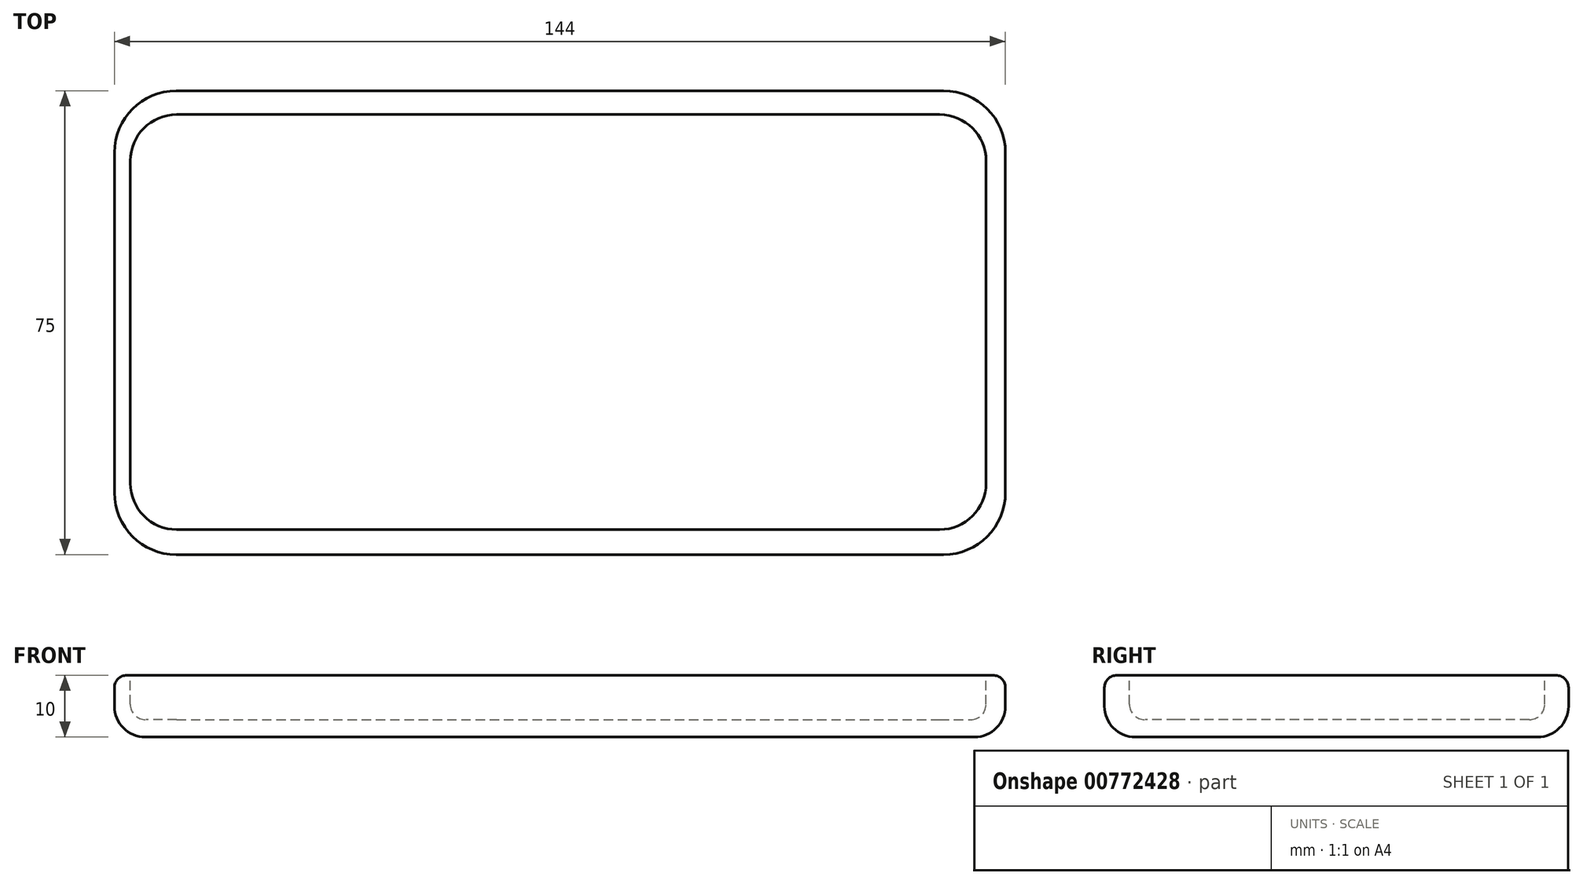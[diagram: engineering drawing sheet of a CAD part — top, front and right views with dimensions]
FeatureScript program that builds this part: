
annotation { "Feature Type Name" : "Feature", "Feature Type Description" : "" }
export const myFeature = defineFeature(function(context is Context, id is Id, definition is map)
    precondition{}
    {
        {
            var Q0;
            Q0=qCreatedBy(makeId("Top.planeOp"),FACE);
            var sketch = newSketch(context, id + "F0", { "sketchPlane" : qUnion([Q0])});
            skLineSegment(sketch, "E0.bottom", {"start": v(-137.75, 28.6) * mm, "end": v(6.25, 28.6) * mm});
            skLineSegment(sketch, "E0.top", {"start": v(-137.75, -43.4) * mm, "end": v(6.25, -43.4) * mm});
            skLineSegment(sketch, "E0.left", {"start": v(-137.75, 28.6) * mm, "end": v(-137.75, -43.4) * mm});
            skLineSegment(sketch, "E0.right", {"start": v(6.25, 28.6) * mm, "end": v(6.25, -43.4) * mm});
            skSolve(sketch);
        }
        {
            var Q0;
            Q0=makeQuery(id+"F0.imprint","IMPRINT",FACE,{"disambiguationData":[TD([[makeQuery(id+"F0.imprint","IMPRINT",EDGE,{"derivedFrom":sQuery(id+"F0.wireOp",EDGE,"E0.bottom")}),-1.0]])]});
            extrude(context, id + "F1", {"entities" : qUnion([Q0]), "depth" : 10 * mm, "offsetDistance" : 25 * mm});
        }
        {
            var Q0;
            Q0=makeQuery(id+"F1.opExtrude","CAP_FACE",FACE,{"disambiguationData":[OSD([sQuery(id+"F0.wireOp",EDGE,"E0.bottom"),sQuery(id+"F0.wireOp",EDGE,"E0.top"),sQuery(id+"F0.wireOp",EDGE,"E0.left"),sQuery(id+"F0.wireOp",EDGE,"E0.right")])],"isStart":false});
            var sketch = newSketch(context, id + "F2", { "sketchPlane" : qUnion([Q0])});
            skLineSegment(sketch, "E1.bottom", {"start": v(-135.18, 27.75) * mm, "end": v(3.12, 27.75) * mm});
            skLineSegment(sketch, "E1.top", {"start": v(-135.18, -39.35) * mm, "end": v(3.12, -39.35) * mm});
            skLineSegment(sketch, "E1.left", {"start": v(-135.18, 27.75) * mm, "end": v(-135.18, -39.35) * mm});
            skLineSegment(sketch, "E1.right", {"start": v(3.12, 27.75) * mm, "end": v(3.12, -39.35) * mm});
            skSolve(sketch);
        }
        {
            var Q0;
            Q0=makeQuery(id+"F1.opExtrude","SWEPT_FACE",FACE,{"disambiguationData":[OSD([sQuery(id+"F0.wireOp",EDGE,"E0.bottom")])]});
            extrude(context, id + "F3", {"entities" : qUnion([Q0]), "operationType" : NewBodyOperationType.ADD, "depth" : 3 * mm, "offsetDistance" : 25 * mm});
        }
        {
            var Q0;
            Q0=makeQuery(id+"F2.imprint","IMPRINT",FACE,{"disambiguationData":[TD([[makeQuery(id+"F2.imprint","IMPRINT",EDGE,{"derivedFrom":sQuery(id+"F2.wireOp",EDGE,"E1.bottom")}),-1.0]])]});
            extrude(context, id + "F4", {"entities" : qUnion([Q0]), "operationType" : NewBodyOperationType.REMOVE, "oppositeDirection" : true, "depth" : 7.2 * mm, "offsetDistance" : 25 * mm});
        }
        {
            var Q0;
            Q0=makeQuery(id+"F4.boolean.opBoolean","COPY",EDGE,{"derivedFrom":makeQuery(id+"F4.opExtrude","SWEPT_EDGE",EDGE,{"disambiguationData":[OSD([sQuery(id+"F2.wireOp",EDGE,"E1.bottom"),sQuery(id+"F2.wireOp",EDGE,"E1.left")])]})});
            var Q1;
            Q1=makeQuery(id+"F4.boolean.opBoolean","COPY",EDGE,{"derivedFrom":makeQuery(id+"F4.opExtrude","SWEPT_EDGE",EDGE,{"disambiguationData":[OSD([sQuery(id+"F2.wireOp",EDGE,"E1.top"),sQuery(id+"F2.wireOp",EDGE,"E1.left")])]})});
            var Q2;
            Q2=makeQuery(id+"F4.boolean.opBoolean","COPY",EDGE,{"derivedFrom":makeQuery(id+"F4.opExtrude","SWEPT_EDGE",EDGE,{"disambiguationData":[OSD([sQuery(id+"F2.wireOp",EDGE,"E1.top"),sQuery(id+"F2.wireOp",EDGE,"E1.right")])]})});
            var Q3;
            Q3=makeQuery(id+"F4.boolean.opBoolean","COPY",EDGE,{"derivedFrom":makeQuery(id+"F4.opExtrude","SWEPT_EDGE",EDGE,{"disambiguationData":[OSD([sQuery(id+"F2.wireOp",EDGE,"E1.bottom"),sQuery(id+"F2.wireOp",EDGE,"E1.right")])]})});
            fillet(context, id + "F5", {"entities" : qUnion([Q0, Q1, Q2, Q3]), "radius" : 7.5 * mm, "tangentPropagation" : true, "allowEdgeOverflow" : false});
        }
        {
            var Q0;
            Q0=makeQuery(id+"F4.boolean.opBoolean","COPY",EDGE,{"derivedFrom":makeQuery(id+"F4.opExtrude","CAP_EDGE",EDGE,{"disambiguationData":[OSD([sQuery(id+"F2.wireOp",EDGE,"E1.bottom")])],"isStart":false})});
            fillet(context, id + "F6", {"entities" : qUnion([Q0]), "radius" : 2.5 * mm, "tangentPropagation" : true, "allowEdgeOverflow" : false});
        }
        {
            var Q0;
            Q0=makeQuery(id+"F1.opExtrude","SWEPT_EDGE",EDGE,{"disambiguationData":[OSD([sQuery(id+"F0.wireOp",EDGE,"E0.top"),sQuery(id+"F0.wireOp",EDGE,"E0.left")])]});
            var Q1;
            Q1=makeQuery(id+"F1.opExtrude","SWEPT_EDGE",EDGE,{"disambiguationData":[OSD([sQuery(id+"F0.wireOp",EDGE,"E0.top"),sQuery(id+"F0.wireOp",EDGE,"E0.right")])]});
            var Q2;
            Q2=makeQuery(id+"F3.opExtrude","CAP_EDGE",EDGE,{"disambiguationData":[OSD([sQuery(id+"F0.wireOp",EDGE,"E0.bottom"),sQuery(id+"F0.wireOp",EDGE,"E0.right")])],"isStart":false});
            var Q3;
            Q3=makeQuery(id+"F3.opExtrude","CAP_EDGE",EDGE,{"disambiguationData":[OSD([sQuery(id+"F0.wireOp",EDGE,"E0.bottom"),sQuery(id+"F0.wireOp",EDGE,"E0.left")])],"isStart":false});
            fillet(context, id + "F7", {"entities" : qUnion([Q0, Q1, Q2, Q3]), "radius" : 10 * mm, "tangentPropagation" : true, "allowEdgeOverflow" : false});
        }
        {
            var Q0;
            Q0=makeQuery(id+"F1.opExtrude","CAP_EDGE",EDGE,{"disambiguationData":[OSD([sQuery(id+"F0.wireOp",EDGE,"E0.top")])],"isStart":false});
            var Q1;
            {var subQ0=sQuery(id+"F0.wireOp",EDGE,"E0.bottom");Q1=makeQuery(id+"F3.opExtrude","CAP_EDGE",EDGE,{"disambiguationData":[OSD([subQ0]),TDD([makeQuery(id+"F1.opExtrude","CAP_EDGE",EDGE,{"disambiguationData":[OSD([subQ0])],"isStart":false})])],"isStart":false});}
            var Q2;
            {var subQ0=sQuery(id+"F0.wireOp",EDGE,"E0.left");var subQ1=sQuery(id+"F0.wireOp",EDGE,"E0.bottom");Q2=makeQuery(id+"F3.boolean.opBoolean","MERGE",EDGE,{"derivedFrom":[makeQuery(id+"F1.opExtrude","CAP_EDGE",EDGE,{"disambiguationData":[OSD([subQ0])],"isStart":false}),makeQuery(id+"F3.opExtrude","SWEPT_EDGE",EDGE,{"disambiguationData":[OSD([subQ1,subQ0]),TDD([makeQuery(id+"F1.opExtrude","CAP_VERTEX",VERTEX,{"disambiguationData":[OSD([subQ1,subQ0])],"isStart":false})])]})]});}
            fillet(context, id + "F8", {"entities" : qUnion([Q0, Q1, Q2]), "radius" : 2 * mm, "tangentPropagation" : true, "allowEdgeOverflow" : false});
        }
        {
            var Q0;
            {var subQ0=sQuery(id+"F0.wireOp",EDGE,"E0.bottom");Q0=makeQuery(id+"F3.boolean.opBoolean","MERGE",FACE,{"derivedFrom":[makeQuery(id+"F1.opExtrude","CAP_FACE",FACE,{"disambiguationData":[OSD([subQ0,sQuery(id+"F0.wireOp",EDGE,"E0.top"),sQuery(id+"F0.wireOp",EDGE,"E0.left"),sQuery(id+"F0.wireOp",EDGE,"E0.right")])],"isStart":true}),makeQuery(id+"F3.opExtrude","SWEPT_FACE",FACE,{"disambiguationData":[OSD([subQ0]),TDD([makeQuery(id+"F1.opExtrude","CAP_EDGE",EDGE,{"disambiguationData":[OSD([subQ0])],"isStart":true})])]})]});}
            fillet(context, id + "F9", {"entities" : qUnion([Q0]), "radius" : 5 * mm, "tangentPropagation" : true, "allowEdgeOverflow" : false});
        }
    });
